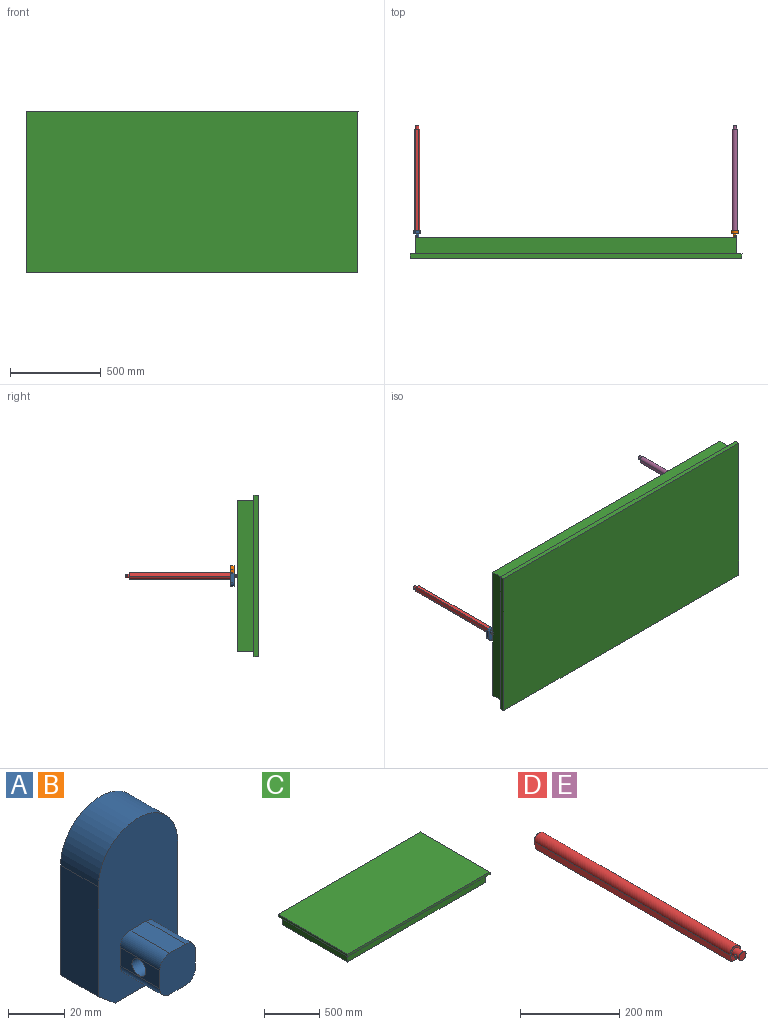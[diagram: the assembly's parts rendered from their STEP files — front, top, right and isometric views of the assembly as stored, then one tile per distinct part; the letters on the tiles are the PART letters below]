
ASSEMBLY  parts=5 mates=4
PART A: 18 faces, bbox 40x39x75 mm
  f0: plane 75x40mm, normal (0,-1,0), area 2466.3mm2, adj f1,f2,f3,f4,f5,f7,f8,f9
  f1: plane 23x19mm, normal (0,0,-1), area 437mm2, adj f0,f2,f5,f6
  f2: plane 19x8.5mm, normal (0.64,0,-0.77), area 209.2mm2, adj f0,f1,f3,f6
  f3: plane 48x19mm, normal (1,0,0), area 912mm2, adj f0,f2,f6,f17
  f4: plane 48x19mm, normal (-1,0,0), area 912mm2, adj f0,f5,f6,f17
  f5: plane 19x8.5mm, normal (-0.64,0,-0.77), area 209.2mm2, adj f0,f1,f4,f6
  f6: plane 75x40mm, normal (0,1,0), area 2768.8mm2, adj f1,f2,f3,f4,f5,f17
  f7: plane 20x8mm, normal (0,0,1), area 160mm2, adj f0,f11,f13,f16
  f8: plane 20x8mm, normal (-1,0,0), area 121.5mm2, adj f0,f11,f12,f13,f14
  f9: plane 20x8mm, normal (0,0,-1), area 160mm2, adj f0,f11,f14,f15
  f10: plane 20x8mm, normal (1,0,0), area 121.5mm2, adj f0,f11,f12,f15,f16
  f11: plane 18x18mm, normal (0,-1,0), area 302.5mm2, adj f7,f8,f9,f10,f13,f14,f15,f16
  f12: cylinder r=3.5mm len=18mm, axis (1,0,0), area 395.8mm2, adj f8,f10
  f13: cylinder r=5mm len=20mm, axis (0,-1,0), area 157.1mm2, adj f0,f7,f8,f11
  f14: cylinder r=5mm len=20mm, axis (0,1,0), area 157.1mm2, adj f0,f8,f9,f11
  f15: cylinder r=5mm len=20mm, axis (0,-1,0), area 157.1mm2, adj f0,f9,f10,f11
  f16: cylinder r=5mm len=20mm, axis (0,1,0), area 157.1mm2, adj f0,f7,f10,f11
  f17: cylinder r=20mm len=40mm, axis (0,-1,0), area 1193.8mm2, adj f0,f3,f4,f6
PART B: same geometry as A
PART C: 16 faces, bbox 1830x890x115.4 mm
  f0: plane 1770x830mm, normal (0,0,-1), area 97356mm2, adj f7,f8,f9,f10,f11,f12,f13,f14
  f1: plane 1830x25.4mm, normal (0,1,0), area 46482mm2, adj f2,f4,f5,f6
  f2: plane 890x25.4mm, normal (-1,0,0), area 22606mm2, adj f1,f3,f5,f6
  f3: plane 1830x25.4mm, normal (0,-1,0), area 46482mm2, adj f2,f4,f5,f6
  f4: plane 890x25.4mm, normal (1,0,0), area 22606mm2, adj f1,f3,f5,f6
  f5: plane 1830x890mm, normal (0,0,-1), area 159600mm2, adj f1,f2,f3,f4,f7,f8,f9,f10
  f6: plane 1830x890mm, normal (0,0,1), area 1628700mm2, adj f1,f2,f3,f4
  f7: plane 1770x90mm, normal (0,-1,0), area 159300mm2, adj f0,f5,f8,f10
  f8: plane 830x90mm, normal (-1,0,0), area 74700mm2, adj f0,f5,f7,f9
  f9: plane 1770x90mm, normal (0,1,0), area 159300mm2, adj f0,f5,f8,f10
  f10: plane 830x90mm, normal (1,0,0), area 74700mm2, adj f0,f5,f7,f9
  f11: plane 1732x90mm, normal (0,1,0), area 155880mm2, adj f0,f12,f14,f15
  f12: plane 792x90mm, normal (1,0,0), area 71280mm2, adj f0,f11,f13,f15
  f13: plane 1732x90mm, normal (0,-1,0), area 155880mm2, adj f0,f12,f14,f15
  f14: plane 792x90mm, normal (-1,0,0), area 71280mm2, adj f0,f11,f13,f15
  f15: plane 1732x792mm, normal (0,0,-1), area 1371744mm2, adj f11,f12,f13,f14
PART D: 9 faces, bbox 30x579.8x35 mm
  f0: cylinder r=10mm len=21mm, axis (0,1,0), area 1241.1mm2, adj f3,f7,f8
  f1: plane 558.8x20mm, normal (0,0,-1), area 11176mm2, adj f2,f3,f4,f5
  f2: plane 35x30mm, normal (0,1,0), area 853.4mm2, adj f1,f4,f5,f6
  f3: plane 35x30mm, normal (0,-1,0), area 539.3mm2, adj f0,f1,f4,f5,f6
  f4: plane 558.8x20mm, normal (-0.97,0,-0.24), area 11520mm2, adj f1,f2,f3,f6
  f5: plane 558.8x20mm, normal (0.97,0,-0.24), area 11520mm2, adj f1,f2,f3,f6
  f6: cylinder r=15mm len=558.8mm, axis (0,-1,0), area 26332.8mm2, adj f2,f3,f4,f5
  f7: plane 20x20mm, normal (0,-1,0), area 314.2mm2, adj f0
  f8: cylinder r=3.5mm len=20mm, axis (1,0,0), area 425.6mm2, adj f0
PART E: same geometry as D
PLACE A rot(axis=(0,-1,0),180deg) t=(-1147.79,-345.13,155.12)mm
PLACE B t=(603.31,-345.13,117.12)mm
PLACE C rot(axis=(1,0,0),90deg) t=(-272.29,-480.53,136.12)mm
PLACE D rot(axis=(-1,0,0),180deg) t=(-1147.79,232.67,155.12)mm
PLACE E rot(axis=(0,0,1),180deg) t=(603.31,232.67,117.12)mm
MATE fastened C.f0 <-> B.f11  axis (0,1,0) through (593.71,-365.13,136.12)mm
MATE fastened D.f2 <-> A.f6  axis (0,1,0) through (-1147.79,-326.13,155.12)mm
MATE fastened A.f11 <-> C.f0  axis (0,1,0) through (-1138.29,-365.13,136.12)mm
MATE fastened B.f6 <-> E.f2  axis (0,1,0) through (603.31,-326.13,117.12)mm
